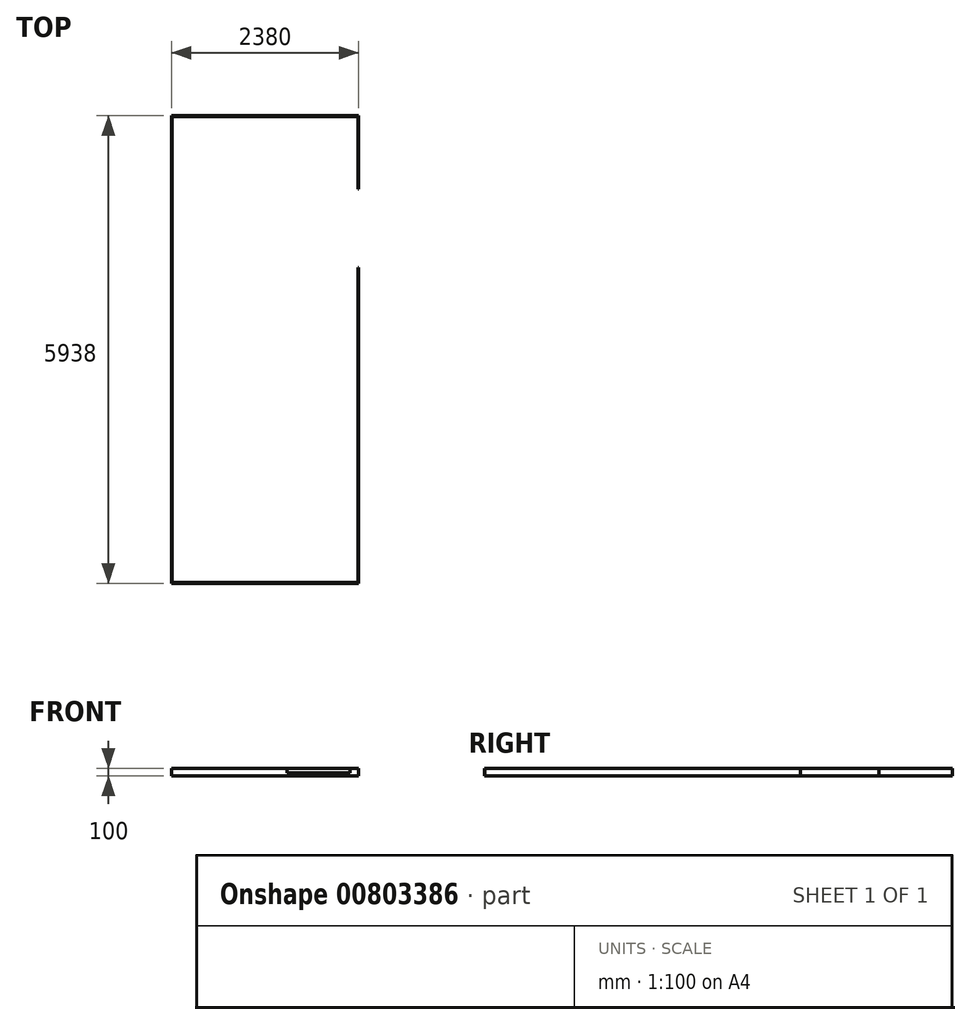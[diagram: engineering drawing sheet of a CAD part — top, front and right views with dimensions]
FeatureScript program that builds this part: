
annotation { "Feature Type Name" : "Feature", "Feature Type Description" : "" }
export const myFeature = defineFeature(function(context is Context, id is Id, definition is map)
    precondition{}
    {
        {
            var Q0;
            Q0=qCreatedBy(makeId("Top.planeOp"),FACE);
            var sketch = newSketch(context, id + "F0", { "sketchPlane" : qUnion([Q0])});
            skLineSegment(sketch, "E0.bottom", {"start": v(0, 0) * mm, "end": v(2380, 0) * mm});
            skLineSegment(sketch, "E0.top", {"start": v(0, 5938) * mm, "end": v(2380, 5938) * mm});
            skLineSegment(sketch, "E0.left", {"start": v(0, 0) * mm, "end": v(0, 5938) * mm});
            skLineSegment(sketch, "E0.right", {"start": v(2380, 0) * mm, "end": v(2380, 5938) * mm});
            skLineSegment(sketch, "E1.bottom", {"start": v(10, 10) * mm, "end": v(2370, 10) * mm});
            skLineSegment(sketch, "E1.top", {"start": v(10, 5928) * mm, "end": v(2370, 5928) * mm});
            skLineSegment(sketch, "E1.left", {"start": v(10, 10) * mm, "end": v(10, 5928) * mm});
            skLineSegment(sketch, "E1.right", {"start": v(2370, 10) * mm, "end": v(2370, 5928) * mm});
            skSolve(sketch);
        }
        {
            var Q0;
            Q0=qSketchRegion(id+"F0",true);
            extrude(context, id + "F1", {"entities" : qUnion([Q0]), "depth" : 100 * mm, "offsetDistance" : 25 * mm});
        }
        {
            var Q0;
            Q0=makeQuery(id+"F1.opExtrude","SWEPT_FACE",FACE,{"disambiguationData":[OSD([sQuery(id+"F0.wireOp",EDGE,"E0.right")])]});
            var sketch = newSketch(context, id + "F2", { "sketchPlane" : qUnion([Q0])});
            skLineSegment(sketch, "E2.bottom", {"start": v(4010, 100) * mm, "end": v(5010, 100) * mm});
            skLineSegment(sketch, "E2.top", {"start": v(4010, 0) * mm, "end": v(5010, 0) * mm});
            skLineSegment(sketch, "E2.left", {"start": v(4010, 100) * mm, "end": v(4010, 0) * mm});
            skLineSegment(sketch, "E2.right", {"start": v(5010, 100) * mm, "end": v(5010, 0) * mm});
            skSolve(sketch);
        }
        {
            var Q0;
            Q0=makeQuery(id+"F2.imprint","IMPRINT",FACE,{"disambiguationData":[TD([[makeQuery(id+"F2.imprint","IMPRINT",EDGE,{"derivedFrom":sQuery(id+"F2.wireOp",EDGE,"E2.bottom")}),-1.0]])]});
            extrude(context, id + "F3", {"entities" : qUnion([Q0]), "operationType" : NewBodyOperationType.REMOVE, "oppositeDirection" : true, "depth" : 25 * mm, "offsetDistance" : 25 * mm});
        }
        {
            var Q0;
            Q0=makeQuery(id+"F1.opExtrude","SWEPT_FACE",FACE,{"disambiguationData":[OSD([sQuery(id+"F0.wireOp",EDGE,"E0.bottom")])]});
            var sketch = newSketch(context, id + "F4", { "sketchPlane" : qUnion([Q0])});
            skLineSegment(sketch, "E3.bottom", {"start": v(2270, 100) * mm, "end": v(1470, 100) * mm});
            skLineSegment(sketch, "E3.top", {"start": v(2270, 40) * mm, "end": v(1470, 40) * mm});
            skLineSegment(sketch, "E3.left", {"start": v(2270, 100) * mm, "end": v(2270, 40) * mm});
            skLineSegment(sketch, "E3.right", {"start": v(1470, 100) * mm, "end": v(1470, 40) * mm});
            skSolve(sketch);
        }
        {
            var Q0;
            Q0 = qSketchRegion(id + "F4", true);
            extrude(context, id + "F5", {"entities" : qUnion([Q0]), "operationType" : NewBodyOperationType.REMOVE, "oppositeDirection" : true, "depth" : 25 * mm, "offsetDistance" : 25 * mm});
        }
    });
